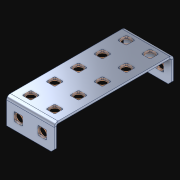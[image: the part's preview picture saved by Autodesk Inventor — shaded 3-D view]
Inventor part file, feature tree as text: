
AUTODESK INVENTOR PART (.ipt)
format: ipt  version: 2021 (Build 250183000, 183)  size: 1,349,632 bytes
history: native  units: in
note: dims shown in document units (in); Inventor stores cm internally (conversion verified against a paired STEP export)
features: extrude x15, other x15, sketch x4, pattern_linear x3
ambient origin geometry x8: Origin, YZ Plane, XZ Plane, XY Plane, X Axis, Y Axis, Z Axis, Center Point
bodies: Solid1 (feature_tree)
feature tree (37):
  pattern_linear  "Rectangular Pattern1"  Spacing1=0.182in  [1 undecoded]
  pattern_linear  "Rectangular Pattern2"  Spacing1=0.046in  [1 undecoded]
  pattern_linear  "Rectangular Pattern3"  Spacing1=0.5in  [1 undecoded]
  extrude  "Extrusion1"  Depth=0.5in
  sketch  "Sketch1"  dims[d0=0.182in]
  other  "Srf1"
  sketch  "Sketch2"  dims[d1=0.046in d2=0.0in]
  other  "Srf2"
  sketch  "Sketch3"  dims[d3=0.182in]
  other  "Srf3"
  other  "Srf4"
  other  "Srf38"
  other  "Srf72"
  other  "Srf73"
  other  "Srf107"
  other  "Srf108"
  other  "Srf142"
  other  "Srf143"
  other  "Srf177"
  other  "Srf178"
  other  "Srf212"
  sketch  "Sketch4"  dims[d4=0.046in d5=0.0in d6=0.182in d7=0.046in d8=0.0in d11=0.5in d12=0.7874in d14=0.5in d15=1.9685in d17=0.5in d18=0.7874in d20=0.5in d21=16.5in d22=0.0in]
  parser-record x1  (decoder bookkeeping rows leaked as tree rows — omitted from the tree; the rows remain in map.json)
  extrude  "ExtrusionSrf1"  Depth=0.5in
  extrude  "ExtrusionSrf2"  Depth=0.5in
  extrude  "ExtrusionSrf3"  Depth=0.5in
  extrude  "ExtrusionSrf4"  Depth=0.5in
  extrude  "ExtrusionSrf38"  Depth=0.5in
  extrude  "ExtrusionSrf72"  TaperAngle=0.0deg  [1 undecoded]
  extrude  "ExtrusionSrf73"  [1 undecoded]
  extrude  "ExtrusionSrf107"  [1 undecoded]
  extrude  "ExtrusionSrf108"  [1 undecoded]
  extrude  "ExtrusionSrf142"  [1 undecoded]
  extrude  "ExtrusionSrf143"  [1 undecoded]
  extrude  "ExtrusionSrf177"  [1 undecoded]
  extrude  "ExtrusionSrf178"  [1 undecoded]
  extrude  "ExtrusionSrf212"  [1 undecoded]
note: 12 required parameter values undecoded (feature->parameter linkage not recoverable at this tier; creation-order binding heuristic only, values carry confidence <= 0.55)
